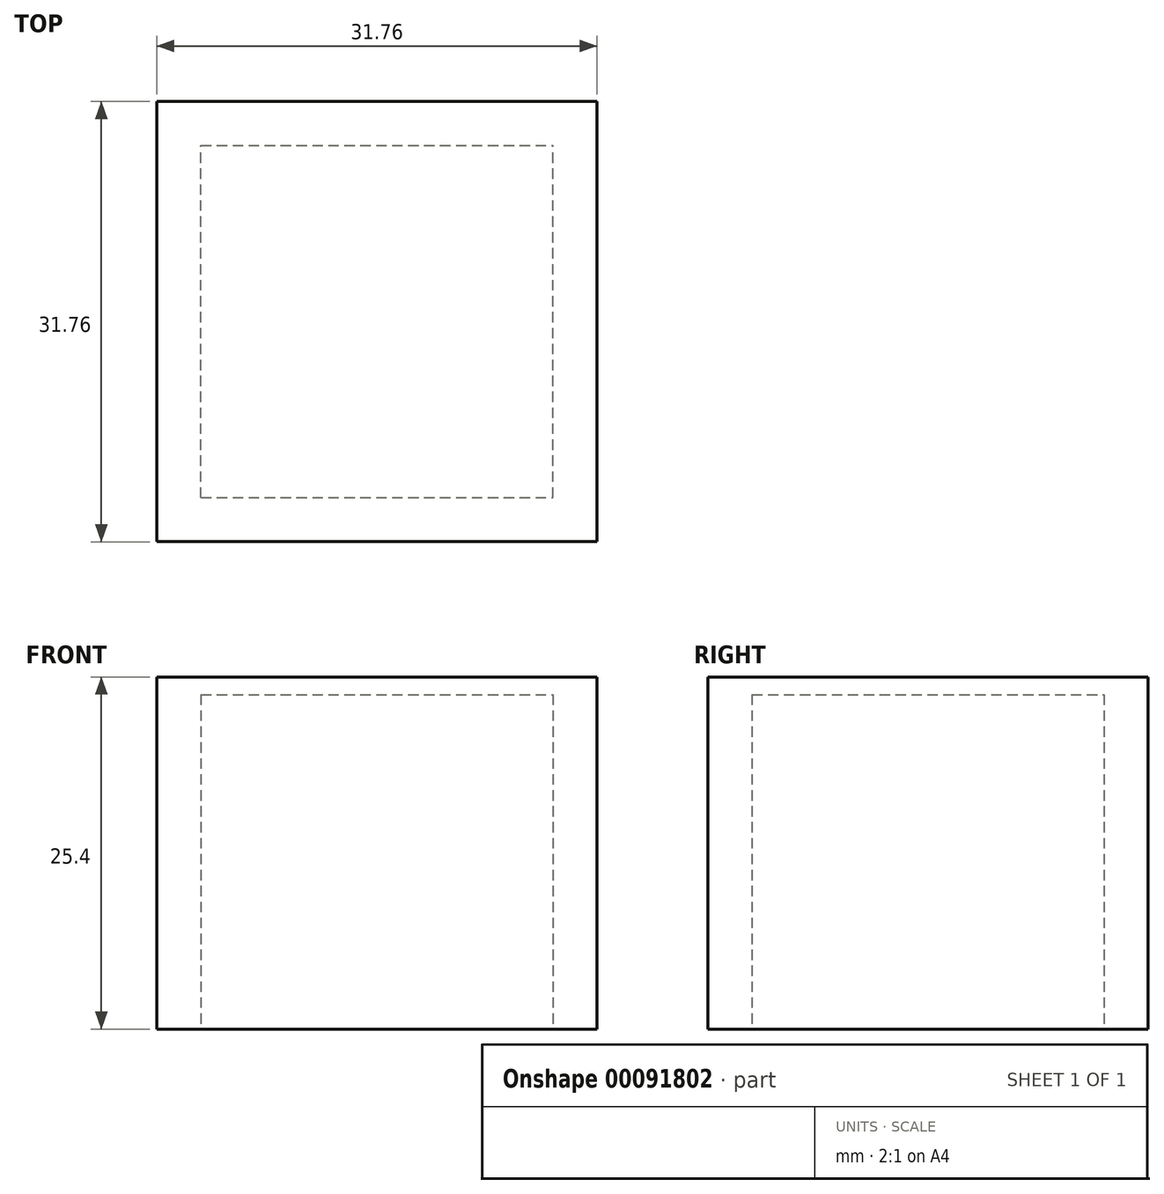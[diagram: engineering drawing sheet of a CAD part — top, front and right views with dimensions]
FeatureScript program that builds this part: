
annotation { "Feature Type Name" : "Feature", "Feature Type Description" : "" }
export const myFeature = defineFeature(function(context is Context, id is Id, definition is map)
    precondition{}
    {
        {
            var Q0;
            Q0=qCreatedBy(makeId("Top.planeOp"),FACE);
            var sketch = newSketch(context, id + "F0", { "sketchPlane" : qUnion([Q0])});
            skLineSegment(sketch, "E0.bottom", {"start": v(-15.88, 15.88) * mm, "end": v(15.88, 15.88) * mm});
            skLineSegment(sketch, "E0.top", {"start": v(-15.88, -15.88) * mm, "end": v(15.88, -15.88) * mm});
            skLineSegment(sketch, "E0.left", {"start": v(-15.88, 15.88) * mm, "end": v(-15.88, -15.88) * mm});
            skLineSegment(sketch, "E0.right", {"start": v(15.88, 15.88) * mm, "end": v(15.88, -15.88) * mm});
            skSolve(sketch);
        }
        {
            var Q0;
            Q0 = qSketchRegion(id + "F0", true);
            extrude(context, id + "F1", {"entities" : qUnion([Q0]), "depth" : 25.4 * mm});
        }
        {
            var Q0;
            Q0=makeQuery(id+"F1.opExtrude","CAP_FACE",FACE,{"disambiguationData":[OSD([sQuery(id+"F0.wireOp",EDGE,"E0.bottom"),sQuery(id+"F0.wireOp",EDGE,"E0.top"),sQuery(id+"F0.wireOp",EDGE,"E0.left"),sQuery(id+"F0.wireOp",EDGE,"E0.right")])],"isStart":true});
            var sketch = newSketch(context, id + "F2", { "sketchPlane" : qUnion([Q0])});
            skLineSegment(sketch, "E1.bottom", {"start": v(-12.7, 12.7) * mm, "end": v(12.7, 12.7) * mm});
            skLineSegment(sketch, "E1.top", {"start": v(-12.7, -12.7) * mm, "end": v(12.7, -12.7) * mm});
            skLineSegment(sketch, "E1.left", {"start": v(-12.7, 12.7) * mm, "end": v(-12.7, -12.7) * mm});
            skLineSegment(sketch, "E1.right", {"start": v(12.7, 12.7) * mm, "end": v(12.7, -12.7) * mm});
            skSolve(sketch);
        }
        {
            var Q0;
            Q0 = qSketchRegion(id + "F2", true);
            extrude(context, id + "F3", {"entities" : qUnion([Q0]), "operationType" : NewBodyOperationType.REMOVE, "oppositeDirection" : true, "depth" : 24.13 * mm});
        }
    });
